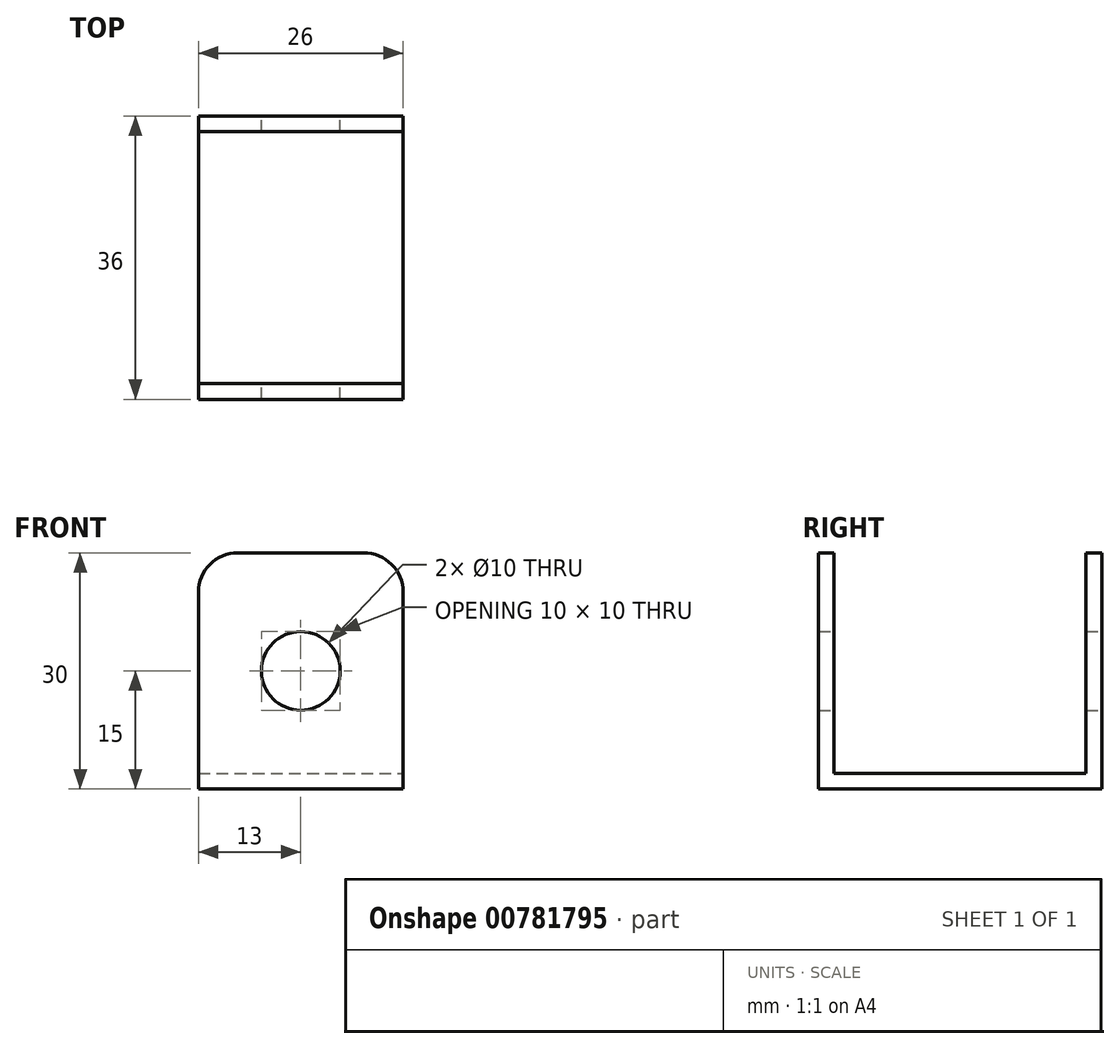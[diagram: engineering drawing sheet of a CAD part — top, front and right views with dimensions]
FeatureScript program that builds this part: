
annotation { "Feature Type Name" : "Feature", "Feature Type Description" : "" }
export const myFeature = defineFeature(function(context is Context, id is Id, definition is map)
    precondition{}
    {
        {
            var Q0;
            Q0=qCreatedBy(makeId("Front.planeOp"),FACE);
            var sketch = newSketch(context, id + "F0", { "sketchPlane" : qUnion([Q0])});
            skLineSegment(sketch, "E0.bottom", {"start": v(13, -15) * mm, "end": v(-13, -15) * mm});
            skLineSegment(sketch, "E0.left", {"start": v(13, -15) * mm, "end": v(13, 15) * mm});
            skLineSegment(sketch, "E0.right", {"start": v(-13, -15) * mm, "end": v(-13, 15) * mm});
            skPoint(sketch, "E0.middle", {"position": v(0, 0) * mm});
            skCircle(sketch, "E1", {"center": v(0, 0) * mm, "radius": 5 * mm});
            skLineSegment(sketch, "E2", {"start": v(-13, 15) * mm, "end": v(13, 15) * mm});
            skSolve(sketch);
        }
        {
            var Q0;
            Q0 = qSketchRegion(id + "F0", true);
            extrude(context, id + "F1", {"entities" : qUnion([Q0]), "endBound" : BoundingType.SYMMETRIC, "depth" : 36 * mm, "offsetDistance" : 25 * mm});
        }
        {
            var Q0;
            Q0=makeQuery(id+"F1.opExtrude","SWEPT_FACE",FACE,{"disambiguationData":[OSD([sQuery(id+"F0.wireOp",EDGE,"E0.left")])]});
            var sketch = newSketch(context, id + "F2", { "sketchPlane" : qUnion([Q0])});
            skLineSegment(sketch, "E3.0", {"start": v(-16, -13) * mm, "end": v(-16, 15) * mm});
            skLineSegment(sketch, "E4.0", {"start": v(-16, -13) * mm, "end": v(16, -13) * mm});
            skLineSegment(sketch, "E5.0", {"start": v(16, -13) * mm, "end": v(16, 15) * mm});
            skSolve(sketch);
        }
        {
            var Q0;
            {var subQ0=sQuery(id+"F2.wireOp",EDGE,"E3.0");Q0=makeQuery(id+"F2.imprint","IMPRINT",FACE,{"disambiguationData":[TD([[makeQuery(id+"F2.imprint","IMPRINT",EDGE,{"derivedFrom":subQ0}),-1.0]])]});}
            extrude(context, id + "F3", {"entities" : qUnion([Q0]), "operationType" : NewBodyOperationType.REMOVE, "endBound" : BoundingType.THROUGH_ALL, "oppositeDirection" : true, "depth" : 25 * mm, "offsetDistance" : 25 * mm});
        }
        {
            var Q0;
            {var subQ0=sQuery(id+"F0.wireOp",EDGE,"E2");var subQ1=sQuery(id+"F0.wireOp",EDGE,"E0.left");Q0=makeQuery(id+"F3.boolean.opBoolean","SPLIT",EDGE,{"disambiguationData":[TD([makeQuery(id+"F3.opExtrude","SWEPT_FACE",FACE,{"disambiguationData":[OSD([sQuery(id+"F2.wireOp",EDGE,"E3.0")])]})])],"derivedFrom":makeQuery(id+"F1.opExtrude","SWEPT_EDGE",EDGE,{"disambiguationData":[OSD([subQ1,subQ0])]})});}
            var Q1;
            {var subQ0=sQuery(id+"F0.wireOp",EDGE,"E2");var subQ1=sQuery(id+"F0.wireOp",EDGE,"E0.right");Q1=makeQuery(id+"F3.boolean.opBoolean","SPLIT",EDGE,{"disambiguationData":[TD([makeQuery(id+"F3.opExtrude","SWEPT_FACE",FACE,{"disambiguationData":[OSD([sQuery(id+"F2.wireOp",EDGE,"E3.0")])]})])],"derivedFrom":makeQuery(id+"F1.opExtrude","SWEPT_EDGE",EDGE,{"disambiguationData":[OSD([subQ1,subQ0])]})});}
            var Q2;
            {var subQ0=sQuery(id+"F0.wireOp",EDGE,"E2");var subQ1=sQuery(id+"F0.wireOp",EDGE,"E0.left");Q2=makeQuery(id+"F3.boolean.opBoolean","SPLIT",EDGE,{"disambiguationData":[TD([makeQuery(id+"F3.opExtrude","SWEPT_FACE",FACE,{"disambiguationData":[OSD([sQuery(id+"F2.wireOp",EDGE,"E5.0")])]})])],"derivedFrom":makeQuery(id+"F1.opExtrude","SWEPT_EDGE",EDGE,{"disambiguationData":[OSD([subQ1,subQ0])]})});}
            var Q3;
            {var subQ0=sQuery(id+"F0.wireOp",EDGE,"E2");var subQ1=sQuery(id+"F0.wireOp",EDGE,"E0.right");Q3=makeQuery(id+"F3.boolean.opBoolean","SPLIT",EDGE,{"disambiguationData":[TD([makeQuery(id+"F3.opExtrude","SWEPT_FACE",FACE,{"disambiguationData":[OSD([sQuery(id+"F2.wireOp",EDGE,"E5.0")])]})])],"derivedFrom":makeQuery(id+"F1.opExtrude","SWEPT_EDGE",EDGE,{"disambiguationData":[OSD([subQ1,subQ0])]})});}
            fillet(context, id + "F4", {"entities" : qUnion([Q0, Q1, Q2, Q3]), "radius" : 5 * mm, "tangentPropagation" : true, "allowEdgeOverflow" : false});
        }
    });
